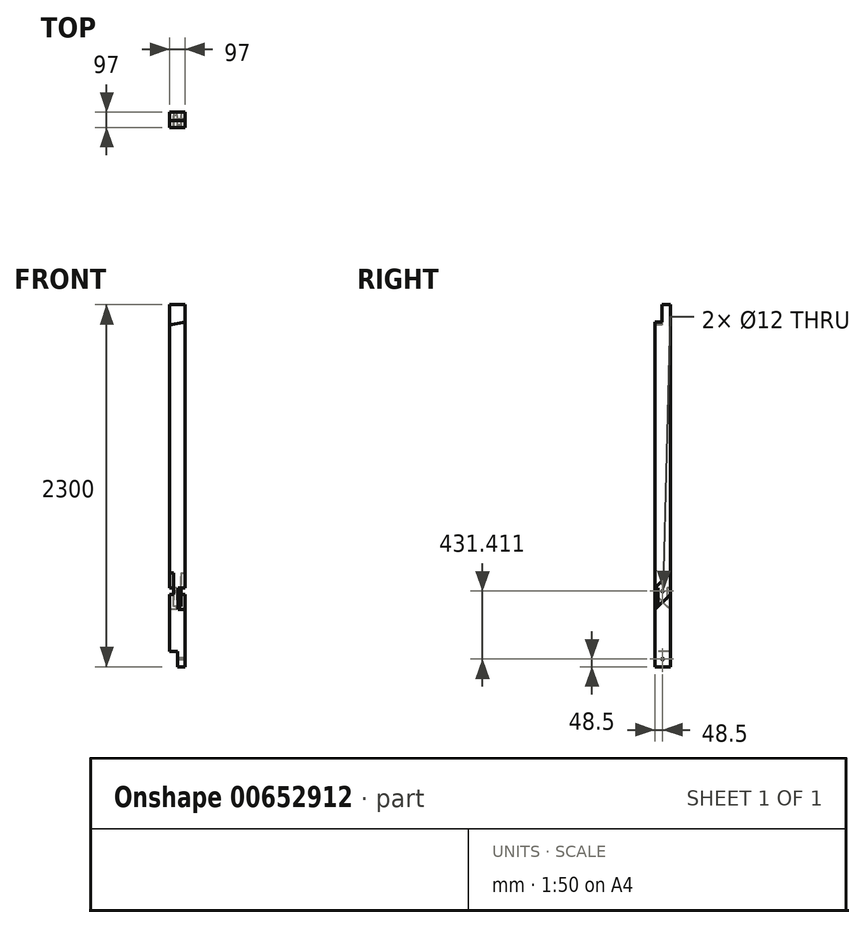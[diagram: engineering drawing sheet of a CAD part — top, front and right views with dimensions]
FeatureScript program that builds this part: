
annotation { "Feature Type Name" : "Feature", "Feature Type Description" : "" }
export const myFeature = defineFeature(function(context is Context, id is Id, definition is map)
    precondition{}
    {
        {
            var Q0;
            Q0=qCreatedBy(makeId("Top.planeOp"),FACE);
            var sketch = newSketch(context, id + "F0", { "sketchPlane" : qUnion([Q0])});
            skLineSegment(sketch, "E0.bottom", {"start": v(48.5, -48.5) * mm, "end": v(-48.5, -48.5) * mm});
            skLineSegment(sketch, "E0.top", {"start": v(48.5, 48.5) * mm, "end": v(-48.5, 48.5) * mm});
            skLineSegment(sketch, "E0.left", {"start": v(48.5, -48.5) * mm, "end": v(48.5, 48.5) * mm});
            skLineSegment(sketch, "E0.right", {"start": v(-48.5, -48.5) * mm, "end": v(-48.5, 48.5) * mm});
            skPoint(sketch, "E0.middle", {"position": v(0, 0) * mm});
            skSolve(sketch);
        }
        {
            var Q0;
            Q0 = qSketchRegion(id + "F0", true);
            extrude(context, id + "F1", {"entities" : qUnion([Q0]), "endBound" : BoundingType.SYMMETRIC, "depth" : 2300 * mm, "offsetDistance" : 25 * mm});
        }
        {
            var Q0;
            Q0=makeQuery(id+"F1.opExtrude","SWEPT_FACE",FACE,{"disambiguationData":[OSD([sQuery(id+"F0.wireOp",EDGE,"E0.right")])]});
            var sketch = newSketch(context, id + "F2", { "sketchPlane" : qUnion([Q0])});
            skLineSegment(sketch, "E1.bottom", {"start": v(-48.5, -1150) * mm, "end": v(48.5, -1150) * mm});
            skLineSegment(sketch, "E1.top", {"start": v(-48.5, -1053) * mm, "end": v(48.5, -1053) * mm});
            skLineSegment(sketch, "E1.left", {"start": v(-48.5, -1150) * mm, "end": v(-48.5, -1053) * mm});
            skLineSegment(sketch, "E1.right", {"start": v(48.5, -1150) * mm, "end": v(48.5, -1053) * mm});
            skSolve(sketch);
        }
        {
            var Q0;
            Q0 = qSketchRegion(id + "F2", true);
            extrude(context, id + "F3", {"entities" : qUnion([Q0]), "operationType" : NewBodyOperationType.REMOVE, "oppositeDirection" : true, "depth" : (97 / 2) * mm, "offsetDistance" : 25 * mm});
        }
        {
            var Q0;
            Q0=makeQuery(id+"F1.opExtrude","SWEPT_FACE",FACE,{"disambiguationData":[OSD([sQuery(id+"F0.wireOp",EDGE,"E0.left")])]});
            var sketch = newSketch(context, id + "F4", { "sketchPlane" : qUnion([Q0])});
            skLineSegment(sketch, "E2", {"start": v(-48.5, -650) * mm, "end": v(-28.5, -650) * mm});
            skLineSegment(sketch, "E3", {"start": v(-28.5, -650) * mm, "end": v(-28.5, -767.18) * mm});
            skLineSegment(sketch, "E4", {"start": v(-28.5, -767.18) * mm, "end": v(-48.5, -787.18) * mm});
            skLineSegment(sketch, "E5", {"start": v(-48.5, -650) * mm, "end": v(-75.32, -676.82) * mm, "construction": true});
            skLineSegment(sketch, "E6", {"start": v(-48.5, -650) * mm, "end": v(-48.5, -787.18) * mm});
            skSolve(sketch);
        }
        {
            var Q0;
            Q0 = qSketchRegion(id + "F4", true);
            extrude(context, id + "F5", {"entities" : qUnion([Q0]), "operationType" : NewBodyOperationType.REMOVE, "oppositeDirection" : true, "depth" : 45 * mm, "offsetDistance" : 25 * mm});
        }
        {
            var Q0;
            Q0=makeQuery(id+"F1.opExtrude","SWEPT_FACE",FACE,{"disambiguationData":[OSD([sQuery(id+"F0.wireOp",EDGE,"E0.left")])]});
            var sketch = newSketch(context, id + "F6", { "sketchPlane" : qUnion([Q0])});
            skLineSegment(sketch, "E7", {"start": v(-48.5, -787.18) * mm, "end": v(48.5, -690.18) * mm});
            skLineSegment(sketch, "E8", {"start": v(-48.5, -650) * mm, "end": v(-48.5, -787.18) * mm});
            skLineSegment(sketch, "E9", {"start": v(-48.5, -787.18) * mm, "end": v(-48.5, -787.18) * mm});
            skLineSegment(sketch, "E10", {"start": v(-48.5, -650) * mm, "end": v(48.5, -553) * mm});
            skLineSegment(sketch, "E11", {"start": v(48.5, -553) * mm, "end": v(48.5, -690.18) * mm});
            skSolve(sketch);
        }
        {
            var Q0;
            Q0 = qSketchRegion(id + "F6", true);
            extrude(context, id + "F7", {"entities" : qUnion([Q0]), "operationType" : NewBodyOperationType.REMOVE, "oppositeDirection" : true, "depth" : 25 * mm, "offsetDistance" : 25 * mm});
        }
        {
            var Q0;
            Q0=makeQuery(id+"F1.opExtrude","SWEPT_FACE",FACE,{"disambiguationData":[OSD([sQuery(id+"F0.wireOp",EDGE,"E0.right")])]});
            var sketch = newSketch(context, id + "F8", { "sketchPlane" : qUnion([Q0])});
            skLineSegment(sketch, "E12", {"start": v(48.5, -553) * mm, "end": v(-48.5, -650) * mm});
            skLineSegment(sketch, "E13", {"start": v(-48.5, -650) * mm, "end": v(-48.5, -787.18) * mm});
            skLineSegment(sketch, "E14", {"start": v(-48.5, -787.18) * mm, "end": v(48.5, -690.18) * mm});
            skLineSegment(sketch, "E15", {"start": v(48.5, -690.18) * mm, "end": v(48.5, -553) * mm});
            skSolve(sketch);
        }
        {
            var Q0;
            Q0 = qSketchRegion(id + "F8", true);
            extrude(context, id + "F9", {"entities" : qUnion([Q0]), "operationType" : NewBodyOperationType.REMOVE, "oppositeDirection" : true, "depth" : 25 * mm, "offsetDistance" : 25 * mm});
        }
        {
            var Q0;
            Q0=makeQuery(id+"F9.boolean.opBoolean","COPY",FACE,{"derivedFrom":makeQuery(id+"F9.opExtrude","CAP_FACE",FACE,{"disambiguationData":[OSD([sQuery(id+"F8.wireOp",EDGE,"E12"),sQuery(id+"F8.wireOp",EDGE,"E13"),sQuery(id+"F8.wireOp",EDGE,"E14"),sQuery(id+"F8.wireOp",EDGE,"E15")])],"isStart":false})});
            var sketch = newSketch(context, id + "F10", { "sketchPlane" : qUnion([Q0])});
            skLineSegment(sketch, "E16", {"start": v(-48.5, -787.18) * mm, "end": v(-48.5, -650) * mm});
            skLineSegment(sketch, "E17", {"start": v(-48.5, -650) * mm, "end": v(-28.5, -650) * mm});
            skLineSegment(sketch, "E18", {"start": v(-28.5, -650) * mm, "end": v(-28.5, -767.18) * mm});
            skLineSegment(sketch, "E19", {"start": v(-28.5, -767.18) * mm, "end": v(-48.5, -787.18) * mm});
            skSolve(sketch);
        }
        {
            var Q0;
            Q0 = qSketchRegion(id + "F10", true);
            extrude(context, id + "F11", {"entities" : qUnion([Q0]), "operationType" : NewBodyOperationType.REMOVE, "oppositeDirection" : true, "depth" : 20 * mm, "offsetDistance" : 25 * mm});
        }
        {
            var Q0;
            Q0=makeQuery(id+"F7.boolean.opBoolean","COPY",FACE,{"derivedFrom":makeQuery(id+"F7.opExtrude","CAP_FACE",FACE,{"disambiguationData":[OSD([sQuery(id+"F6.wireOp",EDGE,"E7"),sQuery(id+"F6.wireOp",EDGE,"E8"),sQuery(id+"F6.wireOp",EDGE,"E10"),sQuery(id+"F6.wireOp",EDGE,"E11")])],"isStart":false})});
            var sketch = newSketch(context, id + "F12", { "sketchPlane" : qUnion([Q0])});
            skCircle(sketch, "E20", {"center": v(0, -670.09) * mm, "radius": 6 * mm});
            skLineSegment(sketch, "E21", {"start": v(0, -601.5) * mm, "end": v(0, -670.09) * mm, "construction": true});
            skLineSegment(sketch, "E22", {"start": v(0, -670.09) * mm, "end": v(0, -738.68) * mm, "construction": true});
            skSolve(sketch);
        }
        {
            var Q0;
            Q0 = qSketchRegion(id + "F12", true);
            extrude(context, id + "F13", {"entities" : qUnion([Q0]), "operationType" : NewBodyOperationType.REMOVE, "endBound" : BoundingType.UP_TO_NEXT, "oppositeDirection" : true, "depth" : 25 * mm, "offsetDistance" : 25 * mm});
        }
        {
            var Q0;
            Q0=makeQuery(id+"F3.boolean.opBoolean","COPY",FACE,{"derivedFrom":makeQuery(id+"F3.opExtrude","CAP_FACE",FACE,{"disambiguationData":[OSD([sQuery(id+"F2.wireOp",EDGE,"E1.bottom"),sQuery(id+"F2.wireOp",EDGE,"E1.top"),sQuery(id+"F2.wireOp",EDGE,"E1.left"),sQuery(id+"F2.wireOp",EDGE,"E1.right")])],"isStart":false})});
            var sketch = newSketch(context, id + "F14", { "sketchPlane" : qUnion([Q0])});
            skLineSegment(sketch, "E23", {"start": v(0, -1053) * mm, "end": v(0, -1101.5) * mm, "construction": true});
            skLineSegment(sketch, "E24", {"start": v(0, -1101.5) * mm, "end": v(0, -1150) * mm, "construction": true});
            skCircle(sketch, "E25", {"center": v(0, -1101.5) * mm, "radius": 6 * mm});
            skSolve(sketch);
        }
        {
            var Q0;
            Q0 = qSketchRegion(id + "F14", true);
            extrude(context, id + "F15", {"entities" : qUnion([Q0]), "operationType" : NewBodyOperationType.REMOVE, "endBound" : BoundingType.UP_TO_NEXT, "oppositeDirection" : true, "depth" : 25 * mm, "offsetDistance" : 25 * mm});
        }
        {
            var Q0;
            Q0=makeQuery(id+"F1.opExtrude","SWEPT_FACE",FACE,{"disambiguationData":[OSD([sQuery(id+"F0.wireOp",EDGE,"E0.bottom")])]});
            var sketch = newSketch(context, id + "F16", { "sketchPlane" : qUnion([Q0])});
            skLineSegment(sketch, "E26.bottom", {"start": v(-48.5, 1150) * mm, "end": v(48.5, 1150) * mm});
            skLineSegment(sketch, "E26.left", {"start": v(-48.5, 1150) * mm, "end": v(-48.5, 1020) * mm});
            skLineSegment(sketch, "E26.right", {"start": v(48.5, 1150) * mm, "end": v(48.5, 1040) * mm});
            skLineSegment(sketch, "E27", {"start": v(-48.5, 1020) * mm, "end": v(48.5, 1040) * mm});
            skSolve(sketch);
        }
        {
            var Q0;
            Q0 = qSketchRegion(id + "F16", true);
            extrude(context, id + "F17", {"entities" : qUnion([Q0]), "operationType" : NewBodyOperationType.REMOVE, "oppositeDirection" : true, "depth" : 45 * mm, "offsetDistance" : 25 * mm});
        }
    });
